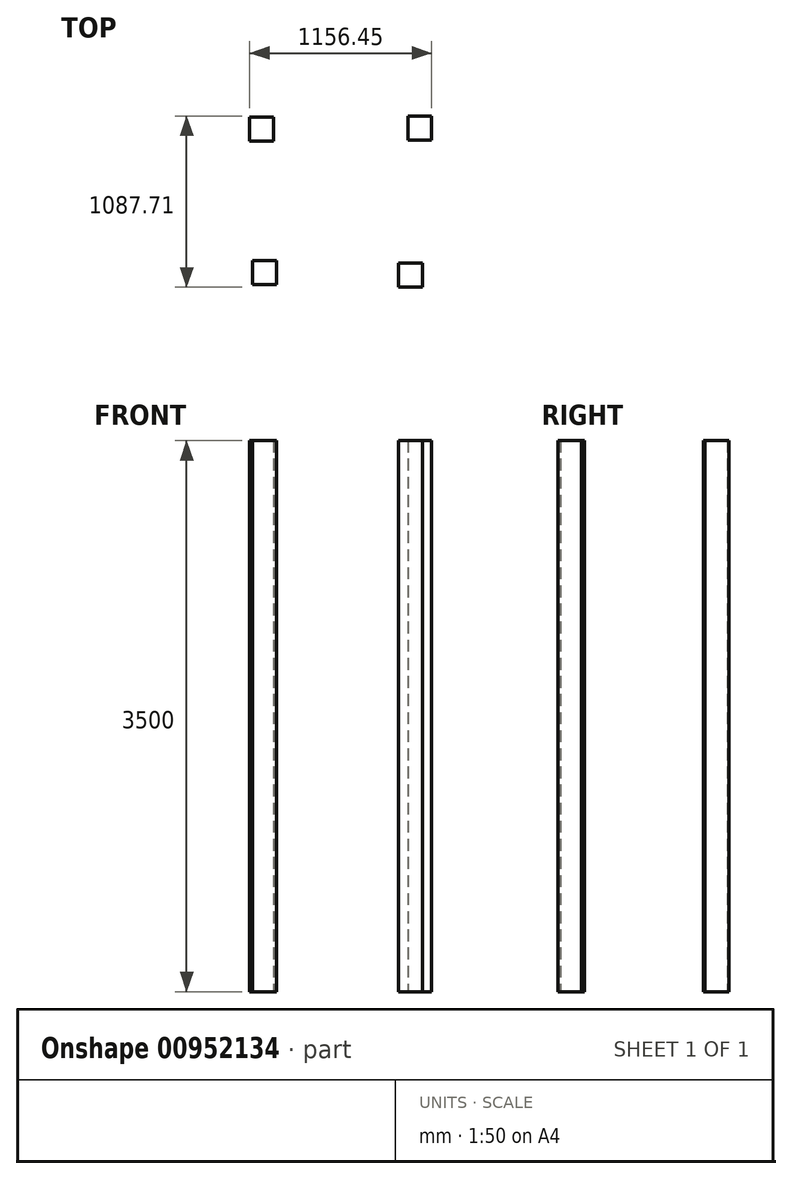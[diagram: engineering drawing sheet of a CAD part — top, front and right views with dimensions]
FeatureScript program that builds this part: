
annotation { "Feature Type Name" : "Feature", "Feature Type Description" : "" }
export const myFeature = defineFeature(function(context is Context, id is Id, definition is map)
    precondition{}
    {
        {
            var Q0;
            Q0=qCreatedBy(makeId("Top.planeOp"),FACE);
            var sketch = newSketch(context, id + "F0", { "sketchPlane" : qUnion([Q0])});
            skLineSegment(sketch, "E0.bottom", {"start": v(-583.84, 545.67) * mm, "end": v(-431.44, 545.67) * mm});
            skLineSegment(sketch, "E0.top", {"start": v(-583.84, 393.27) * mm, "end": v(-431.44, 393.27) * mm});
            skLineSegment(sketch, "E0.left", {"start": v(-583.84, 545.67) * mm, "end": v(-583.84, 393.27) * mm});
            skLineSegment(sketch, "E0.right", {"start": v(-431.44, 545.67) * mm, "end": v(-431.44, 393.27) * mm});
            skLineSegment(sketch, "E1.bottom", {"start": v(-565.91, -362.75) * mm, "end": v(-413.51, -362.75) * mm});
            skLineSegment(sketch, "E1.top", {"start": v(-565.91, -515.15) * mm, "end": v(-413.51, -515.15) * mm});
            skLineSegment(sketch, "E1.left", {"start": v(-565.91, -362.75) * mm, "end": v(-565.91, -515.15) * mm});
            skLineSegment(sketch, "E1.right", {"start": v(-413.51, -362.75) * mm, "end": v(-413.51, -515.15) * mm});
            skLineSegment(sketch, "E2.bottom", {"start": v(420.2, 554.63) * mm, "end": v(572.6, 554.63) * mm});
            skLineSegment(sketch, "E2.top", {"start": v(420.2, 402.23) * mm, "end": v(572.6, 402.23) * mm});
            skLineSegment(sketch, "E2.left", {"start": v(420.2, 554.63) * mm, "end": v(420.2, 402.23) * mm});
            skLineSegment(sketch, "E2.right", {"start": v(572.6, 554.63) * mm, "end": v(572.6, 402.23) * mm});
            skLineSegment(sketch, "E3.bottom", {"start": v(360.44, -380.68) * mm, "end": v(512.84, -380.68) * mm});
            skLineSegment(sketch, "E3.top", {"start": v(360.44, -533.08) * mm, "end": v(512.84, -533.08) * mm});
            skLineSegment(sketch, "E3.left", {"start": v(360.44, -380.68) * mm, "end": v(360.44, -533.08) * mm});
            skLineSegment(sketch, "E3.right", {"start": v(512.84, -380.68) * mm, "end": v(512.84, -533.08) * mm});
            skSolve(sketch);
        }
        {
            var Q0;
            Q0 = qSketchRegion(id + "F0", true);
            extrude(context, id + "F1", {"entities" : qUnion([Q0]), "depth" : 3500 * mm, "offsetDistance" : 25.4 * mm});
        }
    });
